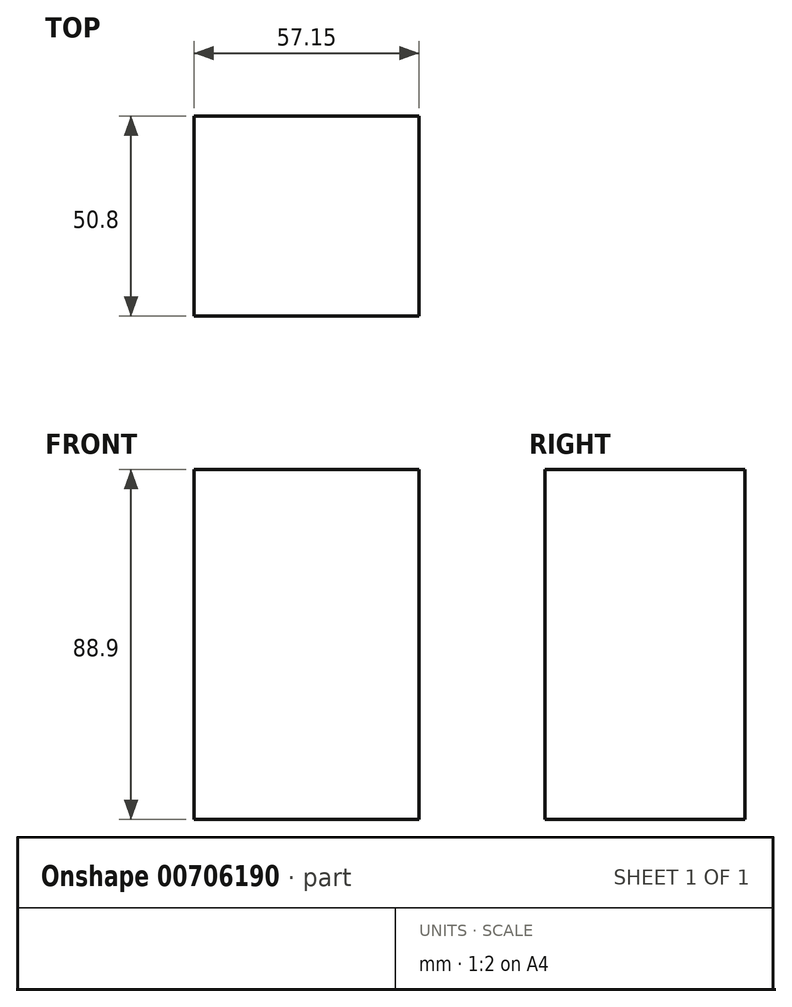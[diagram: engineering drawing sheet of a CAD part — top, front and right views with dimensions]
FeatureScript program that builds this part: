
annotation { "Feature Type Name" : "Feature", "Feature Type Description" : "" }
export const myFeature = defineFeature(function(context is Context, id is Id, definition is map)
    precondition{}
    {
        {
            var Q0;
            Q0=qCreatedBy(makeId("Front.planeOp"),FACE);
            var sketch = newSketch(context, id + "F0", { "sketchPlane" : qUnion([Q0])});
            skLineSegment(sketch, "E0.bottom", {"start": v(-42.5, 38.58) * mm, "end": v(14.64, 38.58) * mm});
            skLineSegment(sketch, "E0.top", {"start": v(-42.5, -50.32) * mm, "end": v(14.64, -50.32) * mm});
            skLineSegment(sketch, "E0.left", {"start": v(-42.5, 38.58) * mm, "end": v(-42.5, -50.32) * mm});
            skLineSegment(sketch, "E0.right", {"start": v(14.64, 38.58) * mm, "end": v(14.64, -50.32) * mm});
            skSolve(sketch);
        }
        {
            var Q0;
            Q0=makeQuery(id+"F0.imprint","IMPRINT",FACE,{"disambiguationData":[TD([[makeQuery(id+"F0.imprint","IMPRINT",EDGE,{"derivedFrom":sQuery(id+"F0.wireOp",EDGE,"E0.bottom")}),-1.0]])]});
            extrude(context, id + "F1", {"entities" : qUnion([Q0]), "depth" : 50.8 * mm, "offsetDistance" : 25.4 * mm});
        }
    });
